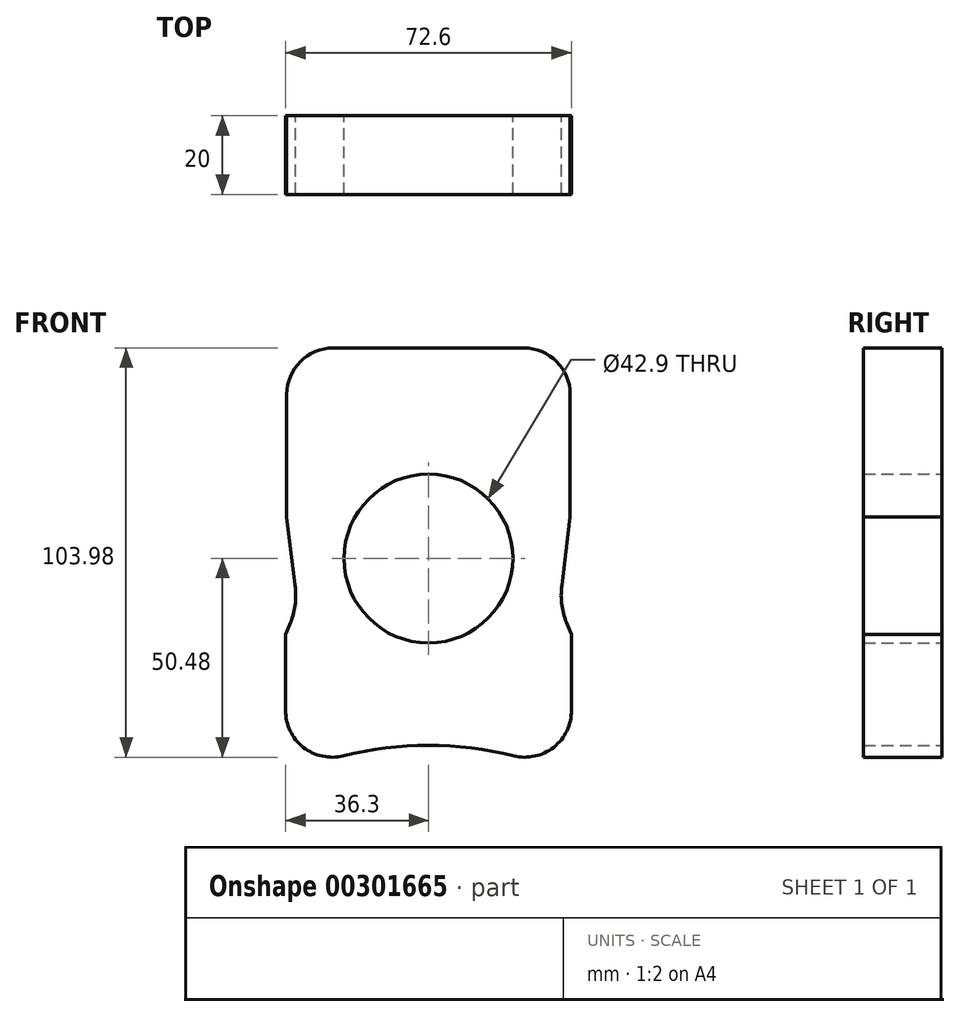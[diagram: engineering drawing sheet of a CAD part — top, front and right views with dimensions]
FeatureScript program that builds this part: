
annotation { "Feature Type Name" : "Feature", "Feature Type Description" : "" }
export const myFeature = defineFeature(function(context is Context, id is Id, definition is map)
    precondition{}
    {
        {
            var Q0;
            Q0=qCreatedBy(makeId("Front.planeOp"),FACE);
            var sketch = newSketch(context, id + "F0", { "sketchPlane" : qUnion([Q0])});
            skLineSegment(sketch, "E0.top", {"start": v(-24.2, 53.5) * mm, "end": v(24.2, 53.5) * mm});
            skPoint(sketch, "E0.middle", {"position": v(0, 0) * mm});
            skCircle(sketch, "E1", {"center": v(0, 0) * mm, "radius": 21.45 * mm});
            skPoint(sketch, "E2.visualSharp", {"position": v(-36, 53.5) * mm});
            skArc(sketch, "E2.filletArc", {"start": v(-24.2, 53.5) * mm, "mid": v(-32.54, 50.04) * mm, "end": v(-36, 41.7) * mm});
            skPoint(sketch, "E3.visualSharp", {"position": v(36, 53.5) * mm});
            skArc(sketch, "E3.filletArc", {"start": v(36, 41.7) * mm, "mid": v(32.54, 50.04) * mm, "end": v(24.2, 53.5) * mm});
            skPoint(sketch, "E4", {"position": v(24.5, -39.5) * mm});
            skLineSegment(sketch, "E5.trimOffspring", {"start": v(36, 10.54) * mm, "end": v(36, 41.7) * mm});
            skLineSegment(sketch, "E6", {"start": v(36.3, -38.68) * mm, "end": v(36.3, -19.24) * mm});
            skPoint(sketch, "E7", {"position": v(53.22, -9.22) * mm});
            skArc(sketch, "E8", {"start": v(33.87, -6.84) * mm, "mid": v(33.91, -11.97) * mm, "end": v(35.3, -16.9) * mm});
            skLineSegment(sketch, "E9", {"start": v(35.3, -16.9) * mm, "end": v(36.3, -19.24) * mm});
            skLineSegment(sketch, "E10", {"start": v(33.87, -6.84) * mm, "end": v(36, 10.54) * mm});
            skPoint(sketch, "E0.bottom.end.orphan", {"position": v(36, -53.5) * mm});
            skPoint(sketch, "E11", {"position": v(0, -138) * mm});
            skArc(sketch, "E12", {"start": v(21.67, -50.13) * mm, "mid": v(10.92, -48.16) * mm, "end": v(0, -47.5) * mm});
            skArc(sketch, "E13", {"start": v(21.67, -50.13) * mm, "mid": v(31.82, -47.93) * mm, "end": v(36.3, -38.57) * mm});
            skPoint(sketch, "E0.left.start.orphan", {"position": v(-36, -53.5) * mm});
            skLineSegment(sketch, "E14.MirrorCS", {"start": v(-35.3, -16.9) * mm, "end": v(-36.3, -19.24) * mm});
            skArc(sketch, "E15.MirrorCS", {"start": v(-33.87, -6.84) * mm, "mid": v(-33.91, -11.97) * mm, "end": v(-35.3, -16.9) * mm});
            skArc(sketch, "E16.MirrorCS", {"start": v(-21.67, -50.13) * mm, "mid": v(-31.82, -47.93) * mm, "end": v(-36.3, -38.57) * mm});
            skLineSegment(sketch, "E17.MirrorCS", {"start": v(-36, 10.54) * mm, "end": v(-36, 41.7) * mm});
            skPoint(sketch, "E18.MirrorP", {"position": v(-24.5, -39.5) * mm});
            skLineSegment(sketch, "E19.MirrorCS", {"start": v(-36.3, -38.68) * mm, "end": v(-36.3, -19.24) * mm});
            skLineSegment(sketch, "E20.MirrorCS", {"start": v(-33.87, -6.84) * mm, "end": v(-36, 10.54) * mm});
            skArc(sketch, "E21.MirrorCS", {"start": v(-21.67, -50.13) * mm, "mid": v(-10.92, -48.16) * mm, "end": v(0, -47.5) * mm});
            skSolve(sketch);
        }
        {
            var Q0;
            Q0 = qSketchRegion(id + "F0", true);
            extrude(context, id + "F1", {"entities" : qUnion([Q0]), "depth" : 20 * mm});
        }
    });
